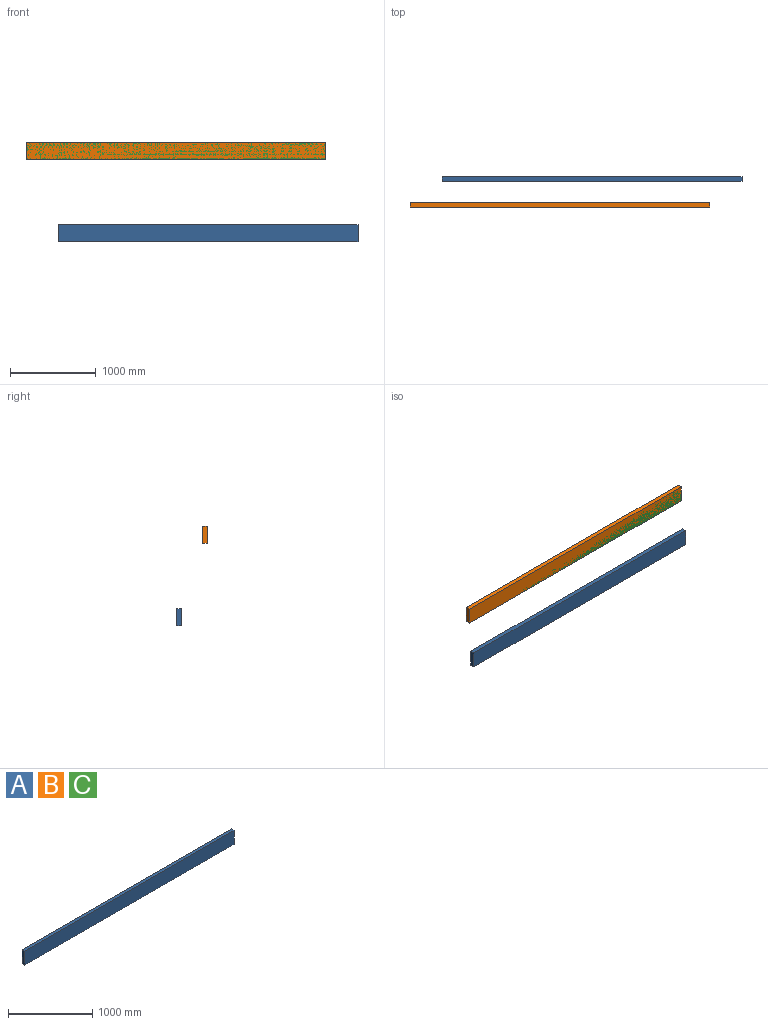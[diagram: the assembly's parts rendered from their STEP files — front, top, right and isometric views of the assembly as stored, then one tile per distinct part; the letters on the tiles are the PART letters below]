
ASSEMBLY  parts=3 mates=1
PART A: 6 faces, bbox 3500x50x200 mm
  f0: plane 3500x50mm, normal (0,0,1), area 175000mm2, adj f1,f3,f4,f5
  f1: plane 3500x200mm, normal (0,-1,0), area 700000mm2, adj f0,f2,f4,f5
  f2: plane 3500x50mm, normal (0,0,-1), area 175000mm2, adj f1,f3,f4,f5
  f3: plane 3500x200mm, normal (0,1,0), area 700000mm2, adj f0,f2,f4,f5
  f4: plane 200x50mm, normal (1,0,0), area 10000mm2, adj f0,f1,f2,f3
  f5: plane 200x50mm, normal (-1,0,0), area 10000mm2, adj f0,f1,f2,f3
PART B: same geometry as A
PART C: same geometry as A
PLACE A t=(-1742.26,267.01,-106.36)mm
PLACE B t=(-2120.38,-36.44,860.58)mm
PLACE C t=(-2120.38,-36.44,860.58)mm
MATE parallel C.f0 <-> B.f0  axis (0,0,1) through (-2120.38,-121.94,1070.33)mm
